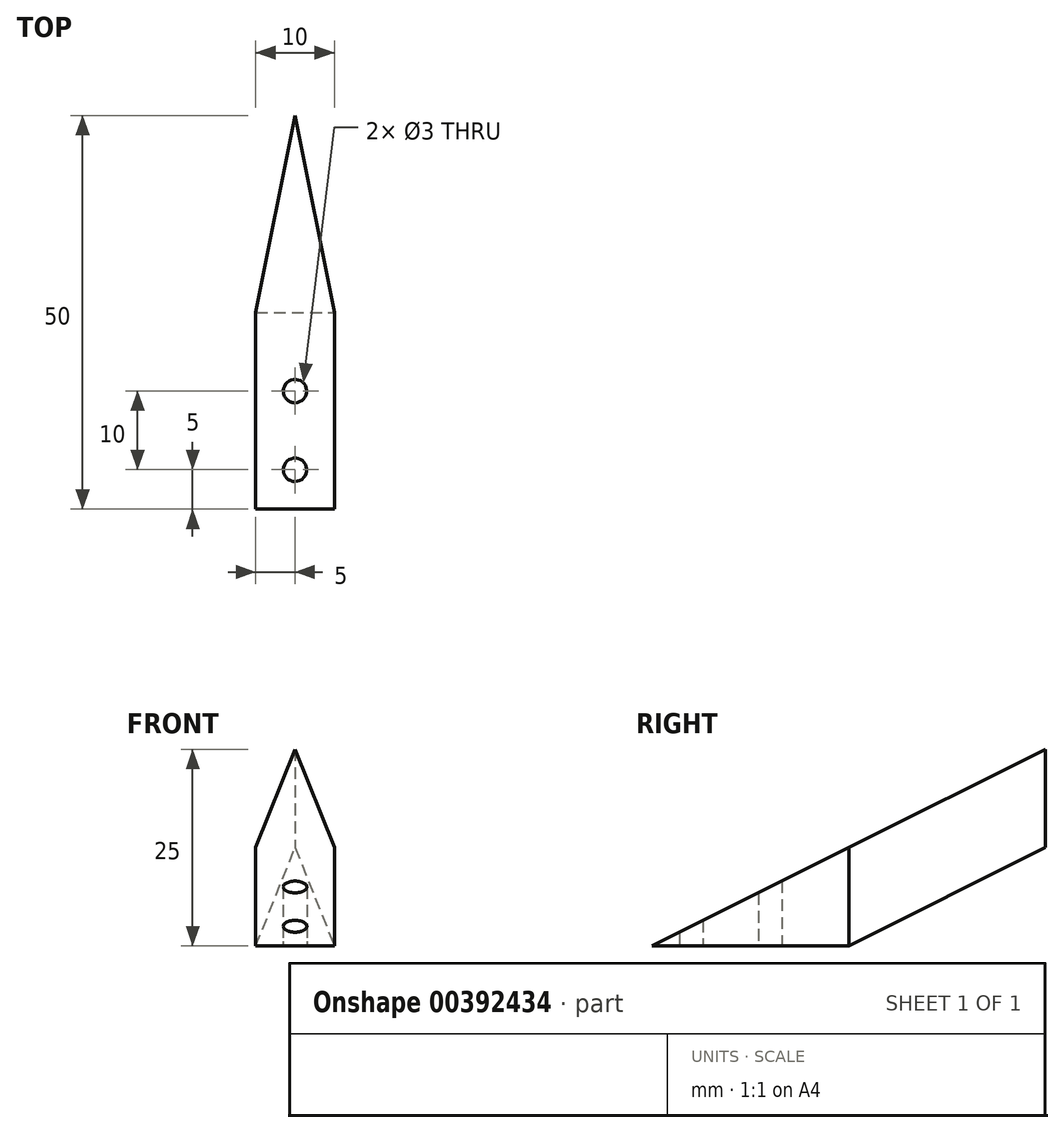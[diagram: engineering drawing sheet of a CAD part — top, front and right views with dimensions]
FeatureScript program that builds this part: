
annotation { "Feature Type Name" : "Feature", "Feature Type Description" : "" }
export const myFeature = defineFeature(function(context is Context, id is Id, definition is map)
    precondition{}
    {
        {
            var Q0;
            Q0=qCreatedBy(makeId("Top.planeOp"),FACE);
            var sketch = newSketch(context, id + "F0", { "sketchPlane" : qUnion([Q0])});
            skLineSegment(sketch, "E0", {"start": v(-5, -50) * mm, "end": v(5, -50) * mm});
            skLineSegment(sketch, "E1", {"start": v(-5, -50) * mm, "end": v(-5, -25) * mm});
            skLineSegment(sketch, "E2", {"start": v(-5, -25) * mm, "end": v(0, 0) * mm});
            skLineSegment(sketch, "E3", {"start": v(5, -50) * mm, "end": v(5, -25) * mm});
            skLineSegment(sketch, "E4", {"start": v(5, -25) * mm, "end": v(0, 0) * mm});
            skSolve(sketch);
        }
        {
            var Q0;
            Q0=makeQuery(id+"F0.imprint","IMPRINT",FACE,{"disambiguationData":[TD([[makeQuery(id+"F0.imprint","IMPRINT",EDGE,{"derivedFrom":sQuery(id+"F0.wireOp",EDGE,"E0")}),1.0]])]});
            extrude(context, id + "F1", {"entities" : qUnion([Q0]), "depth" : 25 * mm});
        }
        {
            var Q0;
            Q0=qCreatedBy(makeId("Right.planeOp"),FACE);
            var sketch = newSketch(context, id + "F2", { "sketchPlane" : qUnion([Q0])});
            skLineSegment(sketch, "E5", {"start": v(0, 0) * mm, "end": v(0, 25) * mm});
            skLineSegment(sketch, "E6", {"start": v(0, 25) * mm, "end": v(-50, 25) * mm});
            skLineSegment(sketch, "E7", {"start": v(-50, 25) * mm, "end": v(-50, 0) * mm});
            skLineSegment(sketch, "E8", {"start": v(-50, 0) * mm, "end": v(0, 25) * mm});
            skLineSegment(sketch, "E9", {"start": v(0, 12.5) * mm, "end": v(-25, 0) * mm});
            skLineSegment(sketch, "E10", {"start": v(-25, 0) * mm, "end": v(0, 0) * mm});
            skSolve(sketch);
        }
        {
            var Q0;
            Q0=makeQuery(id+"F2.imprint","IMPRINT",FACE,{"disambiguationData":[TD([[makeQuery(id+"F2.imprint","IMPRINT",EDGE,{"derivedFrom":sQuery(id+"F2.wireOp",EDGE,"E6")}),1.0]])]});
            var Q1;
            {var subQ2=sQuery(id+"F2.wireOp",EDGE,"E9");Q1=makeQuery(id+"F2.imprint","IMPRINT",FACE,{"disambiguationData":[TD([[makeQuery(id+"F2.imprint","IMPRINT",EDGE,{"derivedFrom":subQ2}),1.0]])]});}
            extrude(context, id + "F3", {"entities" : qUnion([Q0, Q1]), "operationType" : NewBodyOperationType.REMOVE, "endBound" : BoundingType.THROUGH_ALL, "oppositeDirection" : true, "depth" : 25 * mm});
        }
        {
            var Q0;
            Q0=makeQuery(id+"F3.boolean.opBoolean","COPY",FACE,{"derivedFrom":makeQuery(id+"F3.opExtrude","CAP_FACE",FACE,{"disambiguationData":[OSD([sQuery(id+"F2.wireOp",EDGE,"E6"),sQuery(id+"F2.wireOp",EDGE,"E7"),sQuery(id+"F2.wireOp",EDGE,"E8")])],"isStart":true})});
            var Q1;
            Q1=makeQuery(id+"F3.boolean.opBoolean","COPY",FACE,{"derivedFrom":makeQuery(id+"F3.opExtrude","CAP_FACE",FACE,{"disambiguationData":[OSD([sQuery(id+"F2.wireOp",EDGE,"E5"),sQuery(id+"F2.wireOp",EDGE,"E9"),sQuery(id+"F2.wireOp",EDGE,"E10")])],"isStart":true})});
            extrude(context, id + "F4", {"entities" : qUnion([Q0, Q1]), "operationType" : NewBodyOperationType.REMOVE, "endBound" : BoundingType.THROUGH_ALL, "oppositeDirection" : true, "depth" : 25 * mm});
        }
        {
            var Q0;
            Q0=makeQuery(id+"F1.opExtrude","CAP_FACE",FACE,{"disambiguationData":[OSD([sQuery(id+"F0.wireOp",EDGE,"ehulxOQ9-lyk8-lAa2-qF24-xmrEVRH4zTkd"),sQuery(id+"F0.wireOp",EDGE,"E0"),sQuery(id+"F0.wireOp",EDGE,"suWlJ2PU-S0pQ-lx4V-dMZR-5MkWfJLTyj8n")])],"isStart":true});
            var sketch = newSketch(context, id + "F5", { "sketchPlane" : qUnion([Q0])});
            skCircle(sketch, "E11", {"center": v(0, 35) * mm, "radius": 1.5 * mm});
            skCircle(sketch, "E12", {"center": v(0, 45) * mm, "radius": 1.5 * mm});
            skSolve(sketch);
        }
        {
            var Q0;
            Q0=makeQuery(id+"F5.imprint","IMPRINT",FACE,{"disambiguationData":[TD([[makeQuery(id+"F5.imprint","IMPRINT",EDGE,{"derivedFrom":sQuery(id+"F5.wireOp",EDGE,"E11")}),1.0]])]});
            var Q1;
            Q1=makeQuery(id+"F5.imprint","IMPRINT",FACE,{"disambiguationData":[TD([[makeQuery(id+"F5.imprint","IMPRINT",EDGE,{"derivedFrom":sQuery(id+"F5.wireOp",EDGE,"E12")}),1.0]])]});
            extrude(context, id + "F6", {"entities" : qUnion([Q0, Q1]), "operationType" : NewBodyOperationType.REMOVE, "endBound" : BoundingType.THROUGH_ALL, "oppositeDirection" : true, "depth" : 25 * mm});
        }
    });
